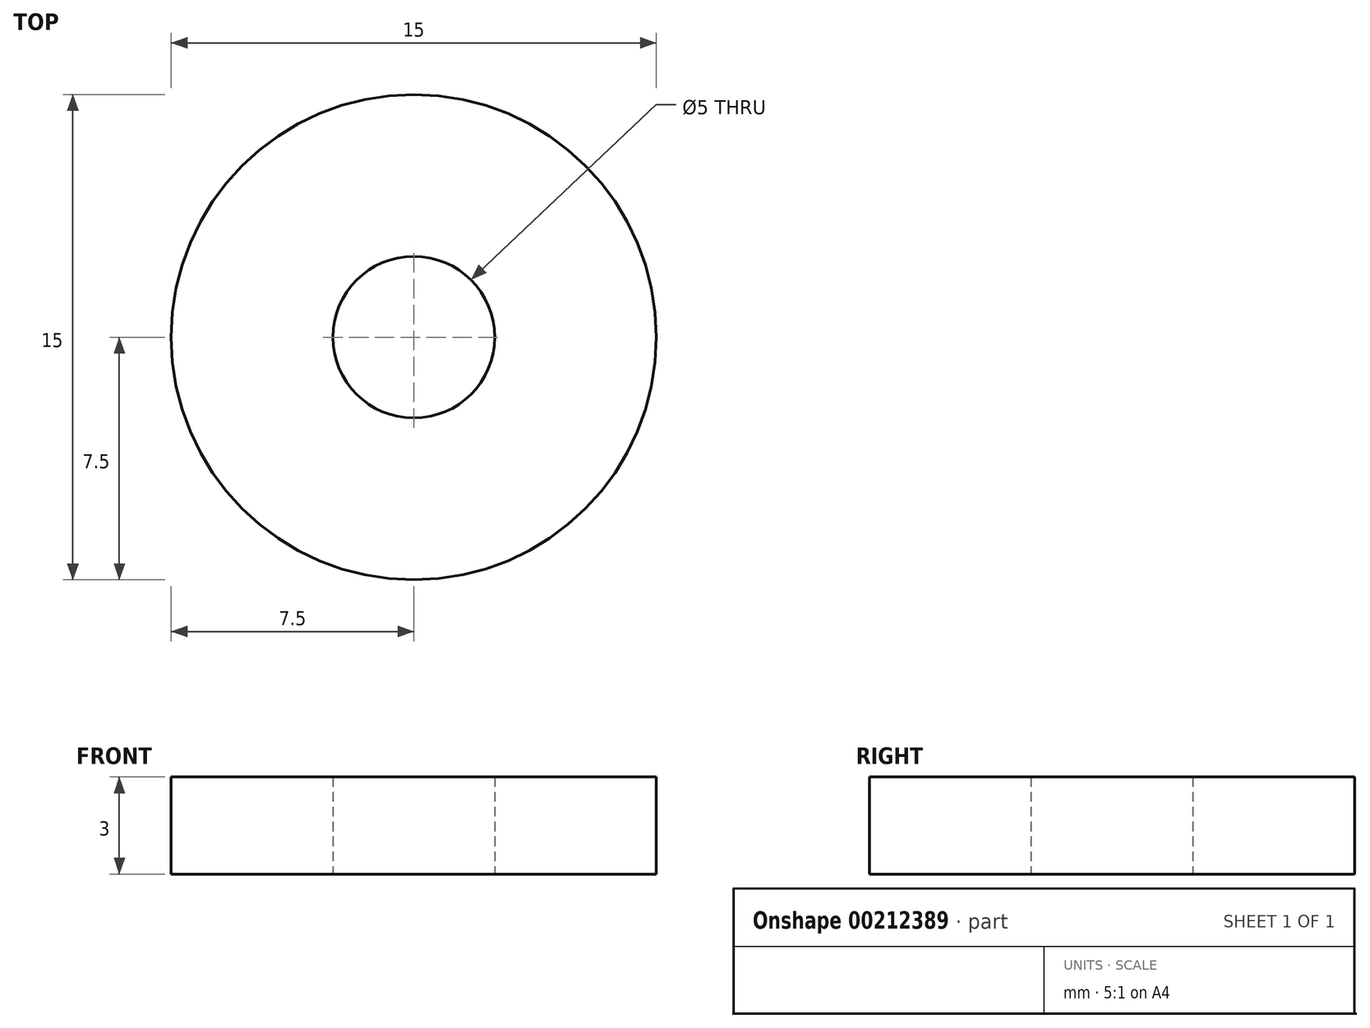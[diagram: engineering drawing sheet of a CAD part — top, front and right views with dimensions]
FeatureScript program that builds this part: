
annotation { "Feature Type Name" : "Feature", "Feature Type Description" : "" }
export const myFeature = defineFeature(function(context is Context, id is Id, definition is map)
    precondition{}
    {
        {
            var Q0;
            Q0=qCreatedBy(makeId("Top.planeOp"),FACE);
            var sketch = newSketch(context, id + "F0", { "sketchPlane" : qUnion([Q0])});
            skCircle(sketch, "E0", {"center": v(0, 0) * mm, "radius": 7.5 * mm});
            skCircle(sketch, "E1", {"center": v(0, 0) * mm, "radius": 2.5 * mm});
            skSolve(sketch);
        }
        {
            var Q0;
            Q0=makeQuery(id+"F0.imprint","IMPRINT",FACE,{"disambiguationData":[TD([[makeQuery(id+"F0.imprint","IMPRINT",EDGE,{"derivedFrom":sQuery(id+"F0.wireOp",EDGE,"E0")}),1.0]])]});
            extrude(context, id + "F1", {"entities" : qUnion([Q0]), "depth" : 3 * mm});
        }
    });
